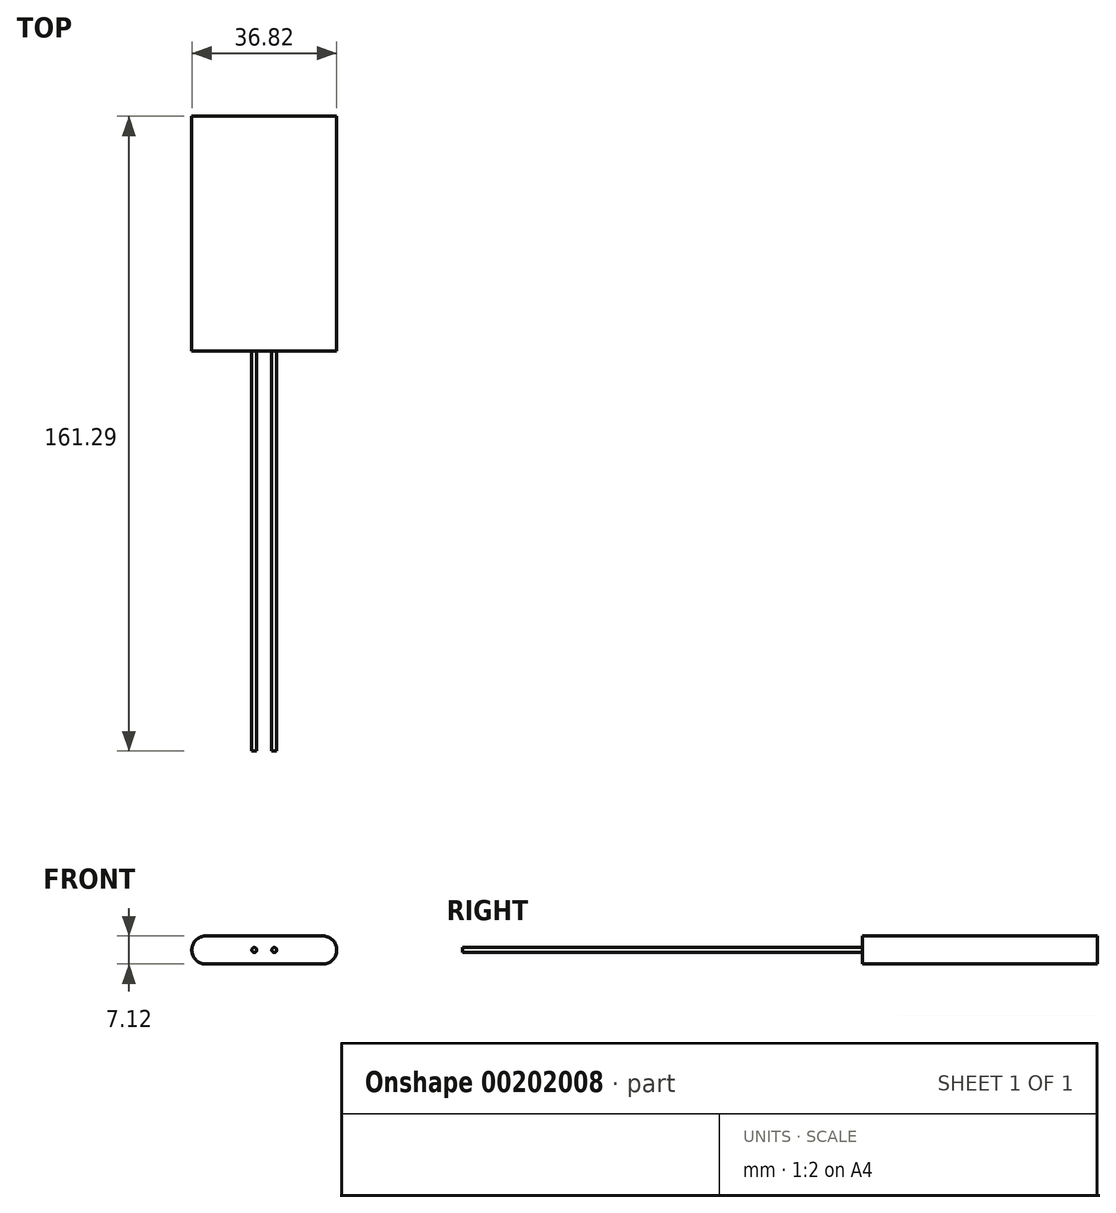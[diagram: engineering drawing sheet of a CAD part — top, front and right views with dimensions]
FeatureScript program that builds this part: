
annotation { "Feature Type Name" : "Feature", "Feature Type Description" : "" }
export const myFeature = defineFeature(function(context is Context, id is Id, definition is map)
    precondition{}
    {
        {
            var Q0;
            Q0=qCreatedBy(makeId("Front.planeOp"),FACE);
            var sketch = newSketch(context, id + "F0", { "sketchPlane" : qUnion([Q0])});
            skLineSegment(sketch, "E0.bottom", {"start": v(-18.41, 3.56) * mm, "end": v(18.41, 3.56) * mm});
            skLineSegment(sketch, "E0.top", {"start": v(-18.41, -3.56) * mm, "end": v(18.41, -3.56) * mm});
            skLineSegment(sketch, "E0.left", {"start": v(-18.41, 3.56) * mm, "end": v(-18.41, -3.56) * mm});
            skLineSegment(sketch, "E0.right", {"start": v(18.41, 3.56) * mm, "end": v(18.41, -3.56) * mm});
            skPoint(sketch, "E0.middle", {"position": v(0, 0) * mm});
            skSolve(sketch);
        }
        {
            var Q0;
            Q0=makeQuery(id+"F0.imprint","IMPRINT",FACE,{"disambiguationData":[TD([[makeQuery(id+"F0.imprint","IMPRINT",EDGE,{"derivedFrom":sQuery(id+"F0.wireOp",EDGE,"E0.bottom")}),-1.0]])]});
            extrude(context, id + "F1", {"entities" : qUnion([Q0]), "oppositeDirection" : true, "depth" : 59.69 * mm});
        }
        {
            var Q0;
            Q0=makeQuery(id+"F1.opExtrude","CAP_FACE",FACE,{"disambiguationData":[OSD([sQuery(id+"F0.wireOp",EDGE,"E0.bottom"),sQuery(id+"F0.wireOp",EDGE,"E0.top"),sQuery(id+"F0.wireOp",EDGE,"E0.left"),sQuery(id+"F0.wireOp",EDGE,"E0.right")])],"isStart":true});
            var sketch = newSketch(context, id + "F2", { "sketchPlane" : qUnion([Q0])});
            skLineSegment(sketch, "E1", {"start": v(-2.54, 0) * mm, "end": v(2.54, 0) * mm, "construction": true});
            skCircle(sketch, "E2", {"center": v(2.54, 0) * mm, "radius": 0.64 * mm});
            skCircle(sketch, "E3", {"center": v(-2.54, 0) * mm, "radius": 0.64 * mm});
            skSolve(sketch);
        }
        {
            var Q0;
            Q0=makeQuery(id+"F2.imprint","IMPRINT",FACE,{"disambiguationData":[TD([[makeQuery(id+"F2.imprint","IMPRINT",EDGE,{"derivedFrom":sQuery(id+"F2.wireOp",EDGE,"E2")}),1.0]])]});
            extrude(context, id + "F3", {"entities" : qUnion([Q0]), "depth" : 101.6 * mm});
        }
        {
            var Q0;
            Q0=makeQuery(id+"F2.imprint","IMPRINT",FACE,{"disambiguationData":[TD([[makeQuery(id+"F2.imprint","IMPRINT",EDGE,{"derivedFrom":sQuery(id+"F2.wireOp",EDGE,"E3")}),1.0]])]});
            extrude(context, id + "F4", {"entities" : qUnion([Q0]), "depth" : 101.6 * mm});
        }
        {
            var Q0;
            Q0=makeQuery(id+"F1.opExtrude","SWEPT_EDGE",EDGE,{"disambiguationData":[OSD([sQuery(id+"F0.wireOp",EDGE,"E0.bottom"),sQuery(id+"F0.wireOp",EDGE,"E0.left")])]});
            var Q1;
            Q1=makeQuery(id+"F1.opExtrude","SWEPT_EDGE",EDGE,{"disambiguationData":[OSD([sQuery(id+"F0.wireOp",EDGE,"E0.top"),sQuery(id+"F0.wireOp",EDGE,"E0.left")])]});
            var Q2;
            Q2=makeQuery(id+"F1.opExtrude","SWEPT_EDGE",EDGE,{"disambiguationData":[OSD([sQuery(id+"F0.wireOp",EDGE,"E0.bottom"),sQuery(id+"F0.wireOp",EDGE,"E0.right")])]});
            var Q3;
            Q3=makeQuery(id+"F1.opExtrude","SWEPT_EDGE",EDGE,{"disambiguationData":[OSD([sQuery(id+"F0.wireOp",EDGE,"E0.top"),sQuery(id+"F0.wireOp",EDGE,"E0.right")])]});
            fillet(context, id + "F5", {"entities" : qUnion([Q0, Q1, Q2, Q3]), "radius" : 3.5 * mm, "tangentPropagation" : true, "allowEdgeOverflow" : false});
        }
    });
